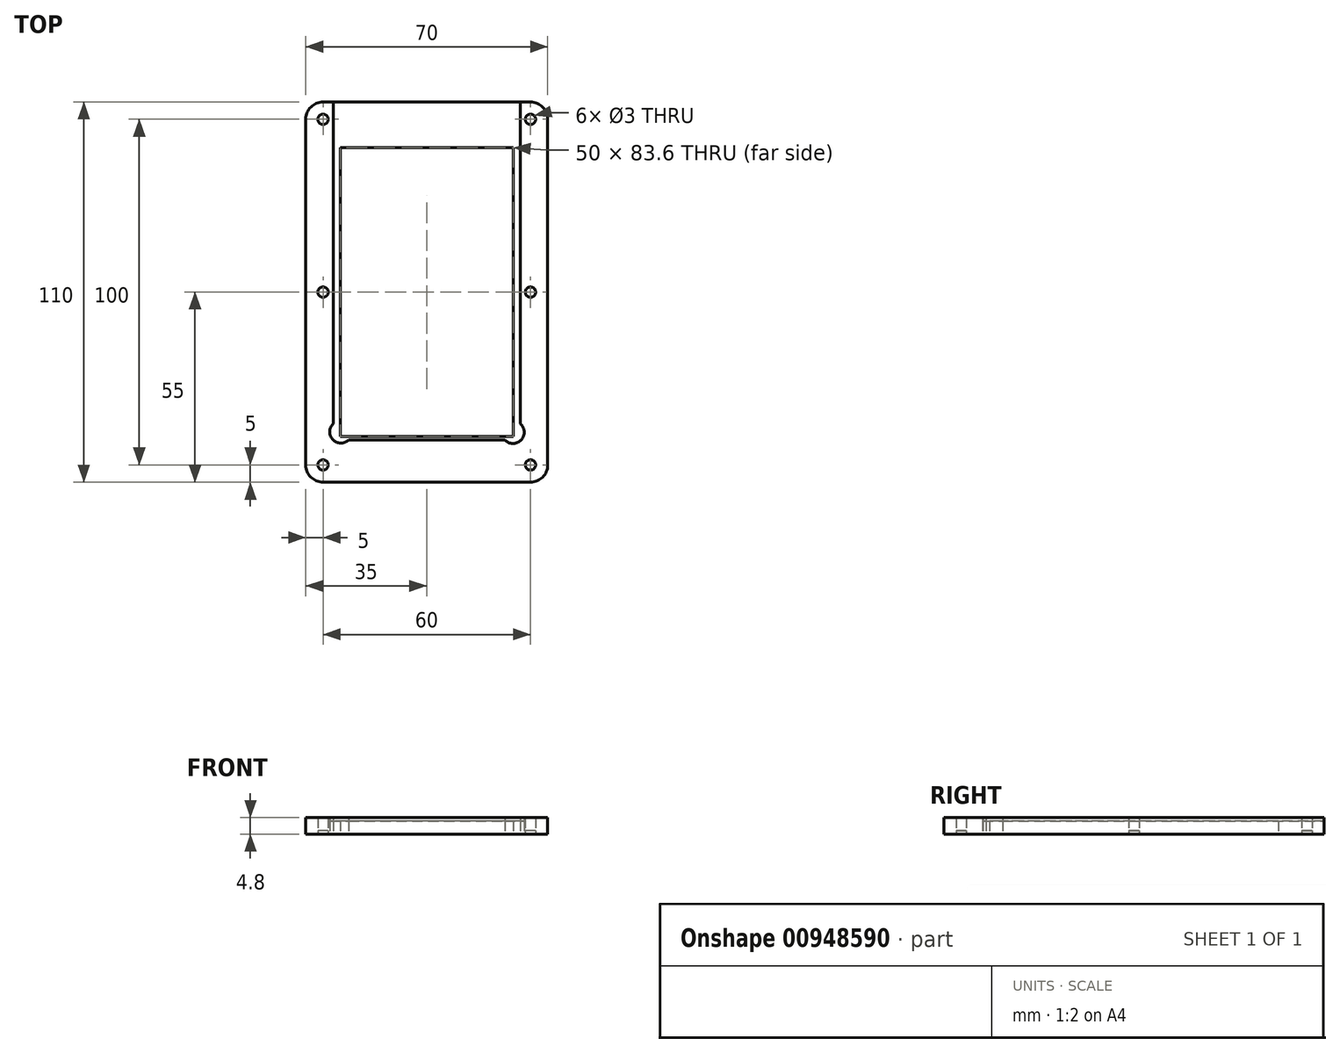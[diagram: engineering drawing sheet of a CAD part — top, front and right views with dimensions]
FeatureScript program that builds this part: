
annotation { "Feature Type Name" : "Feature", "Feature Type Description" : "" }
export const myFeature = defineFeature(function(context is Context, id is Id, definition is map)
    precondition{}
    {
        {
            var Q0;
            Q0=qCreatedBy(makeId("Top.planeOp"),FACE);
            var sketch = newSketch(context, id + "F0", { "sketchPlane" : qUnion([Q0])});
            skLineSegment(sketch, "E0.bottom", {"start": v(30, 55) * mm, "end": v(-30, 55) * mm});
            skLineSegment(sketch, "E0.top", {"start": v(30, -55) * mm, "end": v(-30, -55) * mm});
            skLineSegment(sketch, "E0.left", {"start": v(35, 50) * mm, "end": v(35, -50) * mm});
            skLineSegment(sketch, "E0.right", {"start": v(-35, 50) * mm, "end": v(-35, -50) * mm});
            skPoint(sketch, "E0.middle", {"position": v(0, 0) * mm});
            skLineSegment(sketch, "E1.bottom", {"start": v(25, 41.8) * mm, "end": v(-25, 41.8) * mm});
            skLineSegment(sketch, "E1.top", {"start": v(25, -41.8) * mm, "end": v(-25, -41.8) * mm});
            skLineSegment(sketch, "E1.left", {"start": v(25, 41.8) * mm, "end": v(25, -41.8) * mm});
            skLineSegment(sketch, "E1.right", {"start": v(-25, 41.8) * mm, "end": v(-25, -41.8) * mm});
            skLineSegment(sketch, "E2.top", {"start": v(-27.05, 55) * mm, "end": v(27.05, 55) * mm});
            skLineSegment(sketch, "E2.left", {"start": v(-27.05, 42.8) * mm, "end": v(-27.05, 55) * mm});
            skLineSegment(sketch, "E2.right", {"start": v(27.05, 42.8) * mm, "end": v(27.05, 55) * mm});
            skPoint(sketch, "E3.visualSharp", {"position": v(-35, 55) * mm});
            skArc(sketch, "E3.filletArc", {"start": v(-30, 55) * mm, "mid": v(-33.54, 53.54) * mm, "end": v(-35, 50) * mm});
            skPoint(sketch, "E4.visualSharp", {"position": v(35, 55) * mm});
            skArc(sketch, "E4.filletArc", {"start": v(35, 50) * mm, "mid": v(33.54, 53.54) * mm, "end": v(30, 55) * mm});
            skPoint(sketch, "E5.visualSharp", {"position": v(35, -55) * mm});
            skArc(sketch, "E5.filletArc", {"start": v(30, -55) * mm, "mid": v(33.54, -53.54) * mm, "end": v(35, -50) * mm});
            skPoint(sketch, "E6.visualSharp", {"position": v(-35, -55) * mm});
            skArc(sketch, "E6.filletArc", {"start": v(-35, -50) * mm, "mid": v(-33.54, -53.54) * mm, "end": v(-30, -55) * mm});
            skCircle(sketch, "E7", {"center": v(-30, 50) * mm, "radius": 1.5 * mm});
            skCircle(sketch, "E8", {"center": v(30, 50) * mm, "radius": 1.5 * mm});
            skCircle(sketch, "E9", {"center": v(-30, -50) * mm, "radius": 1.5 * mm});
            skCircle(sketch, "E10", {"center": v(30, -50) * mm, "radius": 1.5 * mm});
            skCircle(sketch, "E11", {"center": v(-30, 0) * mm, "radius": 1.5 * mm});
            skCircle(sketch, "E12", {"center": v(30, 0) * mm, "radius": 1.5 * mm});
            skLineSegment(sketch, "E13.top", {"start": v(-27.05, -42.8) * mm, "end": v(27.05, -42.8) * mm});
            skLineSegment(sketch, "E13.left", {"start": v(-27.05, 55) * mm, "end": v(-27.05, -42.8) * mm});
            skLineSegment(sketch, "E13.right", {"start": v(27.05, 55) * mm, "end": v(27.05, -42.8) * mm});
            skCircle(sketch, "E14", {"center": v(-24.84, -40.44) * mm, "radius": 3.25 * mm});
            skCircle(sketch, "E15", {"center": v(24.94, -40.54) * mm, "radius": 3.25 * mm});
            skSolve(sketch);
        }
        {
            var Q0;
            Q0=makeQuery(id+"F0.imprint","IMPRINT",FACE,{"disambiguationData":[TD([[makeQuery(id+"F0.imprint","IMPRINT",EDGE,{"derivedFrom":sQuery(id+"F0.wireOp",EDGE,"E7")}),1.0]])]});
            var Q1;
            Q1=makeQuery(id+"F0.imprint","IMPRINT",FACE,{"disambiguationData":[TD([[makeQuery(id+"F0.imprint","IMPRINT",EDGE,{"derivedFrom":sQuery(id+"F0.wireOp",EDGE,"E8")}),1.0]])]});
            var Q2;
            Q2=makeQuery(id+"F0.imprint","IMPRINT",FACE,{"disambiguationData":[TD([[makeQuery(id+"F0.imprint","IMPRINT",EDGE,{"derivedFrom":sQuery(id+"F0.wireOp",EDGE,"E12")}),1.0]])]});
            var Q3;
            Q3=makeQuery(id+"F0.imprint","IMPRINT",FACE,{"disambiguationData":[TD([[makeQuery(id+"F0.imprint","IMPRINT",EDGE,{"derivedFrom":sQuery(id+"F0.wireOp",EDGE,"E10")}),1.0]])]});
            var Q4;
            Q4=makeQuery(id+"F0.imprint","IMPRINT",FACE,{"disambiguationData":[TD([[makeQuery(id+"F0.imprint","IMPRINT",EDGE,{"derivedFrom":sQuery(id+"F0.wireOp",EDGE,"E9")}),1.0]])]});
            var Q5;
            Q5=makeQuery(id+"F0.imprint","IMPRINT",FACE,{"disambiguationData":[TD([[makeQuery(id+"F0.imprint","IMPRINT",EDGE,{"derivedFrom":sQuery(id+"F0.wireOp",EDGE,"E11")}),1.0]])]});
            extrude(context, id + "F1", {"entities" : qUnion([Q0, Q1, Q2, Q3, Q4, Q5]), "depth" : 1 * mm, "offsetDistance" : 25 * mm});
        }
        {
            var Q0;
            {var subQ2=sQuery(id+"F0.wireOp",EDGE,"E1.bottom");Q0=makeQuery(id+"F0.imprint","IMPRINT",FACE,{"disambiguationData":[TD([[makeQuery(id+"F0.imprint","IMPRINT",EDGE,{"derivedFrom":subQ2}),-1.0]])]});}
            var Q1;
            {var subQ6=sQuery(id+"F0.wireOp",EDGE,"E1.top");var subQ8=sQuery(id+"F0.wireOp",EDGE,"E1.right");var subQ9=makeQuery(id+"F0.imprint","INTERSECT",VERTEX,{"derivedFrom":[subQ6,subQ8]});Q1=makeQuery(id+"F0.imprint","IMPRINT",FACE,{"disambiguationData":[TD([[makeQuery(id+"F0.imprint","IMPRINT",EDGE,{"disambiguationData":[TD([[subQ9,1.0]])],"derivedFrom":subQ6}),1.0]])]});}
            var Q2;
            {var subQ0=sQuery(id+"F0.wireOp",EDGE,"E13.left");var subQ1=sQuery(id+"F0.wireOp",EDGE,"E13.top");var subQ2=makeQuery(id+"F0.imprint","INTERSECT",VERTEX,{"derivedFrom":[subQ1,subQ0]});Q2=makeQuery(id+"F0.imprint","IMPRINT",FACE,{"disambiguationData":[TD([[makeQuery(id+"F0.imprint","IMPRINT",EDGE,{"disambiguationData":[TD([[subQ2,-1.0]])],"derivedFrom":subQ1}),-1.0]])]});}
            var Q3;
            {var subQ0=sQuery(id+"F0.wireOp",EDGE,"E15");var subQ1=sQuery(id+"F0.wireOp",EDGE,"E1.top");var subQ2=makeQuery(id+"F0.imprint","INTERSECT",VERTEX,{"derivedFrom":[subQ1,subQ0]});Q3=makeQuery(id+"F0.imprint","IMPRINT",FACE,{"disambiguationData":[TD([[makeQuery(id+"F0.imprint","IMPRINT",EDGE,{"disambiguationData":[TD([[subQ2,-1.0]])],"derivedFrom":subQ1}),1.0]])]});}
            var Q4;
            {var subQ5=sQuery(id+"F0.wireOp",EDGE,"E1.left");var subQ6=sQuery(id+"F0.wireOp",EDGE,"E1.top");var subQ7=makeQuery(id+"F0.imprint","INTERSECT",VERTEX,{"derivedFrom":[subQ6,subQ5]});Q4=makeQuery(id+"F0.imprint","IMPRINT",FACE,{"disambiguationData":[TD([[makeQuery(id+"F0.imprint","IMPRINT",EDGE,{"disambiguationData":[TD([[subQ7,-1.0]])],"derivedFrom":subQ6}),1.0]])]});}
            var Q5;
            {var subQ0=sQuery(id+"F0.wireOp",EDGE,"E13.right");var subQ1=sQuery(id+"F0.wireOp",EDGE,"E13.top");var subQ2=makeQuery(id+"F0.imprint","INTERSECT",VERTEX,{"derivedFrom":[subQ1,subQ0]});Q5=makeQuery(id+"F0.imprint","IMPRINT",FACE,{"disambiguationData":[TD([[makeQuery(id+"F0.imprint","IMPRINT",EDGE,{"disambiguationData":[TD([[subQ2,1.0]])],"derivedFrom":subQ1}),-1.0]])]});}
            extrude(context, id + "F2", {"entities" : qUnion([Q0, Q1, Q2, Q3, Q4, Q5]), "depth" : 3.8 * mm, "offsetDistance" : 25 * mm});
        }
        {
            var Q0;
            Q0=makeQuery(id+"F0.imprint","IMPRINT",FACE,{"disambiguationData":[TD([[makeQuery(id+"F0.imprint","IMPRINT",EDGE,{"derivedFrom":sQuery(id+"F0.wireOp",EDGE,"E0.top")}),-1.0]])]});
            extrude(context, id + "F3", {"entities" : qUnion([Q0]), "depth" : 4.8 * mm, "offsetDistance" : 25 * mm});
        }
    });
